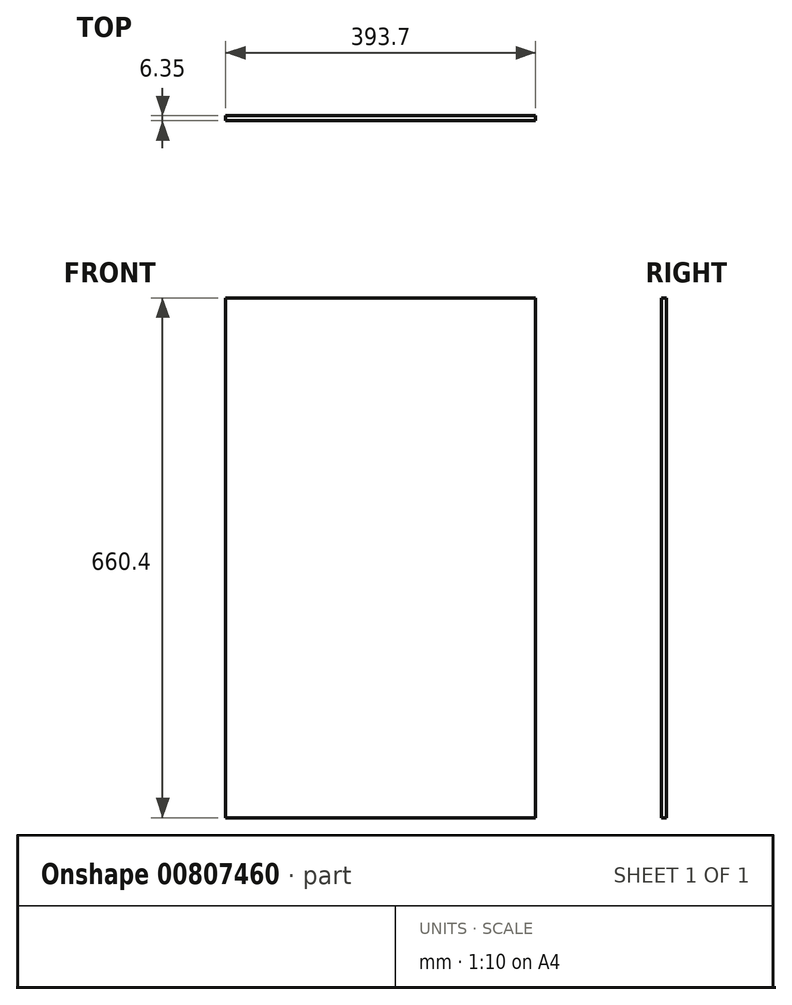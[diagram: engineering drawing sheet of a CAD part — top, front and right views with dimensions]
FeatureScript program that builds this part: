
annotation { "Feature Type Name" : "Feature", "Feature Type Description" : "" }
export const myFeature = defineFeature(function(context is Context, id is Id, definition is map)
    precondition{}
    {
        {
            var Q0;
            Q0=qCreatedBy(makeId("Front.planeOp"),FACE);
            var sketch = newSketch(context, id + "F0", { "sketchPlane" : qUnion([Q0])});
            skLineSegment(sketch, "E0.bottom", {"start": v(0, 0) * mm, "end": v(393.7, 0) * mm});
            skLineSegment(sketch, "E0.top", {"start": v(0, 660.4) * mm, "end": v(393.7, 660.4) * mm});
            skLineSegment(sketch, "E0.left", {"start": v(0, 0) * mm, "end": v(0, 660.4) * mm});
            skLineSegment(sketch, "E0.right", {"start": v(393.7, 0) * mm, "end": v(393.7, 660.4) * mm});
            skSolve(sketch);
        }
        {
            var Q0;
            Q0 = qSketchRegion(id + "F0", true);
            extrude(context, id + "F1", {"entities" : qUnion([Q0]), "depth" : 6.35 * mm, "offsetDistance" : 25.4 * mm});
        }
    });
